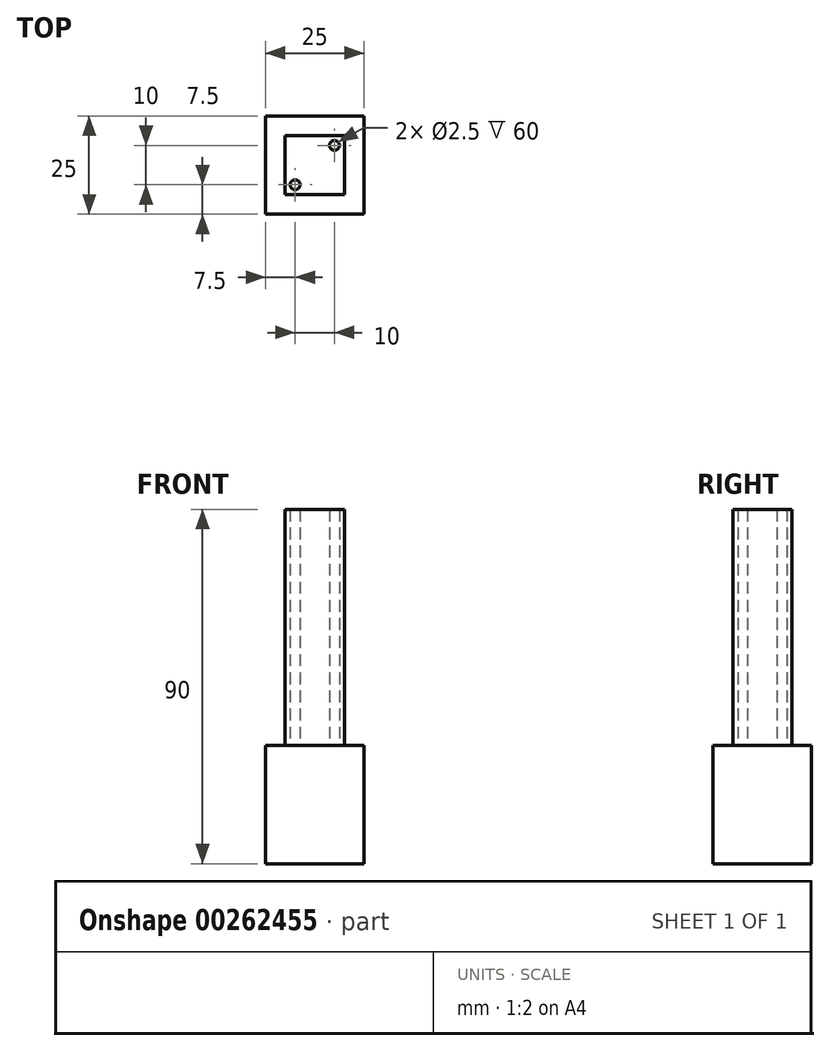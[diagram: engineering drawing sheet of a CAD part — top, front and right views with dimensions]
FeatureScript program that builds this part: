
annotation { "Feature Type Name" : "Feature", "Feature Type Description" : "" }
export const myFeature = defineFeature(function(context is Context, id is Id, definition is map)
    precondition{}
    {
        {
            var Q0;
            Q0=qCreatedBy(makeId("Top.planeOp"),FACE);
            var sketch = newSketch(context, id + "F0", { "sketchPlane" : qUnion([Q0])});
            skLineSegment(sketch, "E0.bottom", {"start": v(-12.5, 12.5) * mm, "end": v(12.5, 12.5) * mm});
            skLineSegment(sketch, "E0.top", {"start": v(-12.5, -12.5) * mm, "end": v(12.5, -12.5) * mm});
            skLineSegment(sketch, "E0.left", {"start": v(-12.5, 12.5) * mm, "end": v(-12.5, -12.5) * mm});
            skLineSegment(sketch, "E0.right", {"start": v(12.5, 12.5) * mm, "end": v(12.5, -12.5) * mm});
            skPoint(sketch, "E0.middle", {"position": v(0, 0) * mm});
            skSolve(sketch);
        }
        {
            var Q0;
            Q0 = qSketchRegion(id + "F0", true);
            extrude(context, id + "F1", {"entities" : qUnion([Q0]), "depth" : 30 * mm});
        }
        {
            var Q0;
            Q0=makeQuery(id+"F1.opExtrude","CAP_FACE",FACE,{"disambiguationData":[OSD([sQuery(id+"F0.wireOp",EDGE,"E0.bottom"),sQuery(id+"F0.wireOp",EDGE,"E0.top"),sQuery(id+"F0.wireOp",EDGE,"E0.left"),sQuery(id+"F0.wireOp",EDGE,"E0.right")])],"isStart":false});
            var sketch = newSketch(context, id + "F2", { "sketchPlane" : qUnion([Q0])});
            skLineSegment(sketch, "E1.bottom", {"start": v(5, -5) * mm, "end": v(-5, -5) * mm, "construction": true});
            skLineSegment(sketch, "E1.top", {"start": v(5, 5) * mm, "end": v(-5, 5) * mm, "construction": true});
            skLineSegment(sketch, "E1.left", {"start": v(5, -5) * mm, "end": v(5, 5) * mm, "construction": true});
            skLineSegment(sketch, "E1.right", {"start": v(-5, -5) * mm, "end": v(-5, 5) * mm, "construction": true});
            skPoint(sketch, "E1.middle", {"position": v(0, 0) * mm});
            skCircle(sketch, "E2", {"center": v(5, -5) * mm, "radius": 1.25 * mm});
            skLineSegment(sketch, "E3", {"start": v(-12.5, 0) * mm, "end": v(12.5, 0) * mm, "construction": true});
            skLineSegment(sketch, "E4", {"start": v(0, 12.5) * mm, "end": v(0, -12.5) * mm, "construction": true});
            skCircle(sketch, "E5.MirrorC", {"center": v(5, 5) * mm, "radius": 1.25 * mm});
            skCircle(sketch, "E6.MirrorC", {"center": v(-5, 5) * mm, "radius": 1.25 * mm});
            skCircle(sketch, "E7.MirrorC", {"center": v(-5, -5) * mm, "radius": 1.25 * mm});
            skLineSegment(sketch, "E8.bottom", {"start": v(7.5, 7.5) * mm, "end": v(-7.5, 7.5) * mm});
            skLineSegment(sketch, "E8.top", {"start": v(7.5, -7.5) * mm, "end": v(-7.5, -7.5) * mm});
            skLineSegment(sketch, "E8.left", {"start": v(7.5, 7.5) * mm, "end": v(7.5, -7.5) * mm});
            skLineSegment(sketch, "E8.right", {"start": v(-7.5, 7.5) * mm, "end": v(-7.5, -7.5) * mm});
            skSolve(sketch);
        }
        {
            var Q0;
            Q0=makeQuery(id+"F2.imprint","IMPRINT",FACE,{"disambiguationData":[TD([[makeQuery(id+"F2.imprint","IMPRINT",EDGE,{"derivedFrom":sQuery(id+"F2.wireOp",EDGE,"E6.MirrorC")}),1.0]])]});
            var Q1;
            Q1=makeQuery(id+"F2.imprint","IMPRINT",FACE,{"disambiguationData":[TD([[makeQuery(id+"F2.imprint","IMPRINT",EDGE,{"derivedFrom":sQuery(id+"F2.wireOp",EDGE,"E5.MirrorC")}),-1.0]])]});
            var Q2;
            Q2=makeQuery(id+"F2.imprint","IMPRINT",FACE,{"disambiguationData":[TD([[makeQuery(id+"F2.imprint","IMPRINT",EDGE,{"derivedFrom":sQuery(id+"F2.wireOp",EDGE,"E7.MirrorC")}),-1.0]])]});
            var Q3;
            Q3=makeQuery(id+"F2.imprint","IMPRINT",FACE,{"disambiguationData":[TD([[makeQuery(id+"F2.imprint","IMPRINT",EDGE,{"derivedFrom":sQuery(id+"F2.wireOp",EDGE,"E2")}),1.0]])]});
            extrude(context, id + "F3", {"entities" : qUnion([Q0, Q1, Q2, Q3]), "operationType" : NewBodyOperationType.ADD, "depth" : 60 * mm});
        }
        {
            var Q0;
            Q0 = qSketchRegion(id + "F2", true);
            extrude(context, id + "F4", {"entities" : qUnion([Q0]), "operationType" : NewBodyOperationType.ADD, "depth" : 0.5 * mm});
        }
    });
